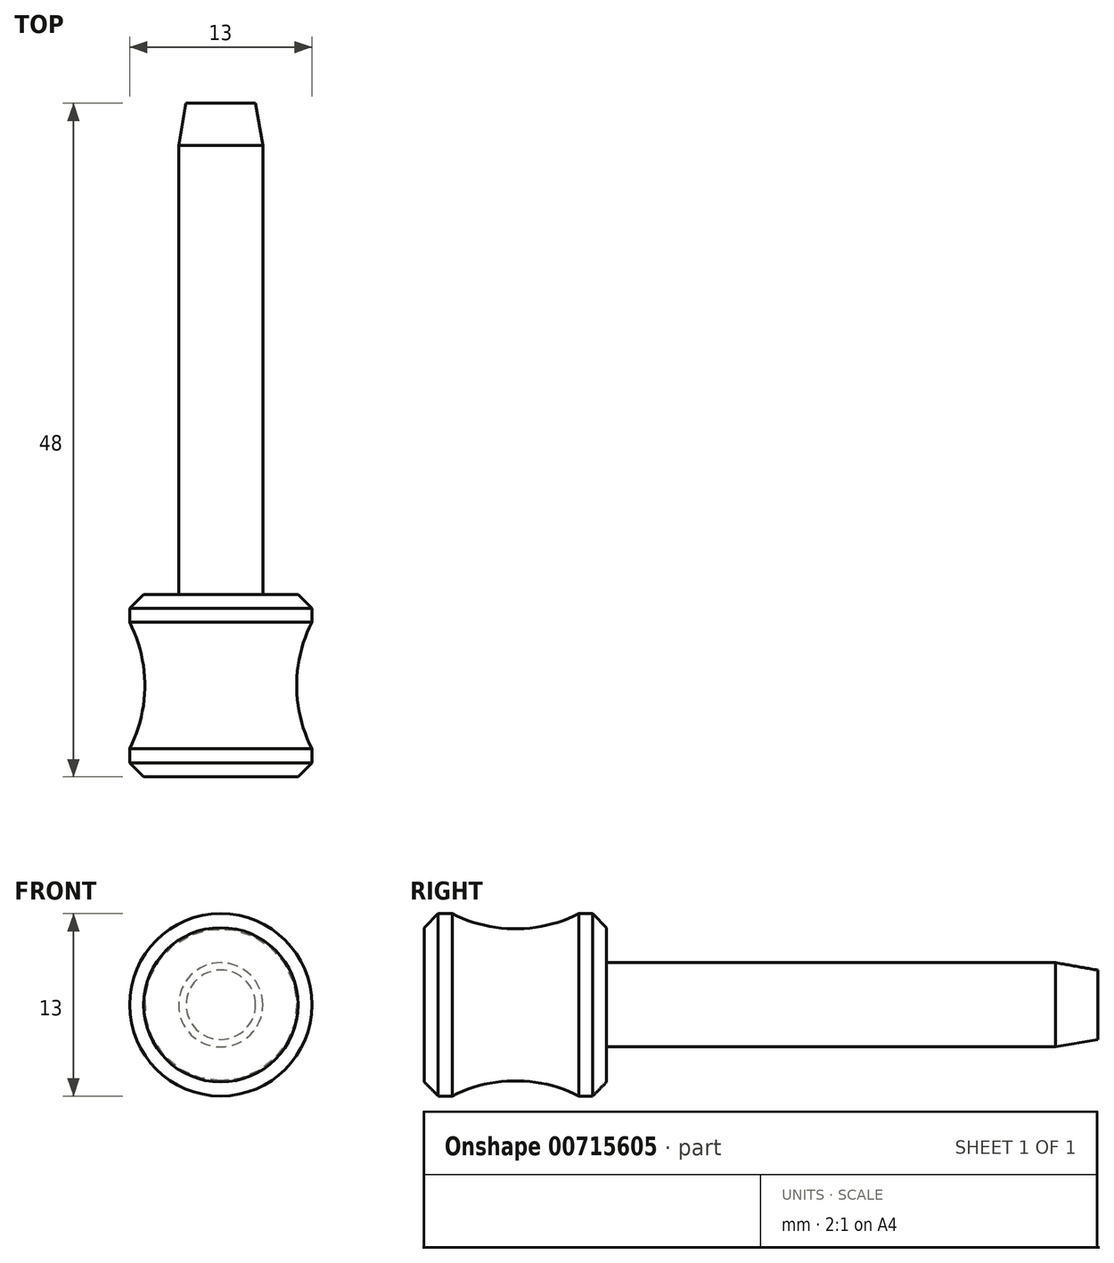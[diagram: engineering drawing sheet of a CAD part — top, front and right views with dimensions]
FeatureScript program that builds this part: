
annotation { "Feature Type Name" : "Feature", "Feature Type Description" : "" }
export const myFeature = defineFeature(function(context is Context, id is Id, definition is map)
    precondition{}
    {
        {
            var Q0;
            Q0=qCreatedBy(makeId("Front.planeOp"),FACE);
            var sketch = newSketch(context, id + "F0", { "sketchPlane" : qUnion([Q0])});
            skCircle(sketch, "E0", {"center": v(0, 0) * mm, "radius": 6.5 * mm});
            skSolve(sketch);
        }
        {
            var Q0;
            Q0 = qSketchRegion(id + "F0", true);
            extrude(context, id + "F1", {"entities" : qUnion([Q0]), "oppositeDirection" : true, "depth" : 13 * mm, "offsetDistance" : 25 * mm});
        }
        {
            var Q0;
            Q0=makeQuery(id+"F1.opExtrude","CAP_FACE",FACE,{"disambiguationData":[OSD([sQuery(id+"F0.wireOp",EDGE,"E0")])],"isStart":false});
            var sketch = newSketch(context, id + "F2", { "sketchPlane" : qUnion([Q0])});
            skCircle(sketch, "E1", {"center": v(0, 0) * mm, "radius": 3 * mm});
            skSolve(sketch);
        }
        {
            var Q0;
            Q0 = qSketchRegion(id + "F2", true);
            extrude(context, id + "F3", {"entities" : qUnion([Q0]), "operationType" : NewBodyOperationType.ADD, "depth" : 35 * mm, "offsetDistance" : 25 * mm});
        }
        {
            var Q0;
            Q0=makeQuery(id+"F3.opExtrude","CAP_EDGE",EDGE,{"disambiguationData":[OSD([sQuery(id+"F2.wireOp",EDGE,"E1")])],"isStart":false});
            chamfer(context, id + "F4", {"entities" : qUnion([Q0]), "chamferType" : ChamferType.OFFSET_ANGLE, "width" : 3 * mm, "oppositeDirection" : true, "angle" : 10 * degree, "tangentPropagation" : true});
        }
        {
            var Q0;
            Q0=makeQuery(id+"F1.opExtrude","CAP_EDGE",EDGE,{"disambiguationData":[OSD([sQuery(id+"F0.wireOp",EDGE,"E0")])],"isStart":false});
            var Q1;
            Q1=makeQuery(id+"F1.opExtrude","CAP_EDGE",EDGE,{"disambiguationData":[OSD([sQuery(id+"F0.wireOp",EDGE,"E0")])],"isStart":true});
            chamfer(context, id + "F5", {"entities" : qUnion([Q0, Q1]), "width" : 1 * mm, "tangentPropagation" : true});
        }
        {
            var Q0;
            Q0=qCreatedBy(makeId("Right.planeOp"),FACE);
            var sketch = newSketch(context, id + "F6", { "sketchPlane" : qUnion([Q0])});
            skArc(sketch, "E2", {"start": v(1, 7.08) * mm, "mid": v(6.5, 5.42) * mm, "end": v(12, 7.07) * mm});
            skLineSegment(sketch, "E3", {"start": v(1, 7.08) * mm, "end": v(12, 7.07) * mm});
            skSolve(sketch);
        }
        {
            var Q0;
            Q0 = qSketchRegion(id + "F6", true);
            var Q1;
            Q1=makeQuery(id+"F3.opExtrude","SWEPT_FACE",FACE,{"disambiguationData":[OSD([sQuery(id+"F2.wireOp",EDGE,"E1")])]});
            revolve(context, id + "F7", {"operationType" : NewBodyOperationType.REMOVE, "surfaceOperationType" : NewSurfaceOperationType.NEW, "entities" : qUnion([Q0]), "axis" : qUnion([Q1]), "revolveType" : RevolveType.FULL, "oppositeDirection" : true});
        }
    });
